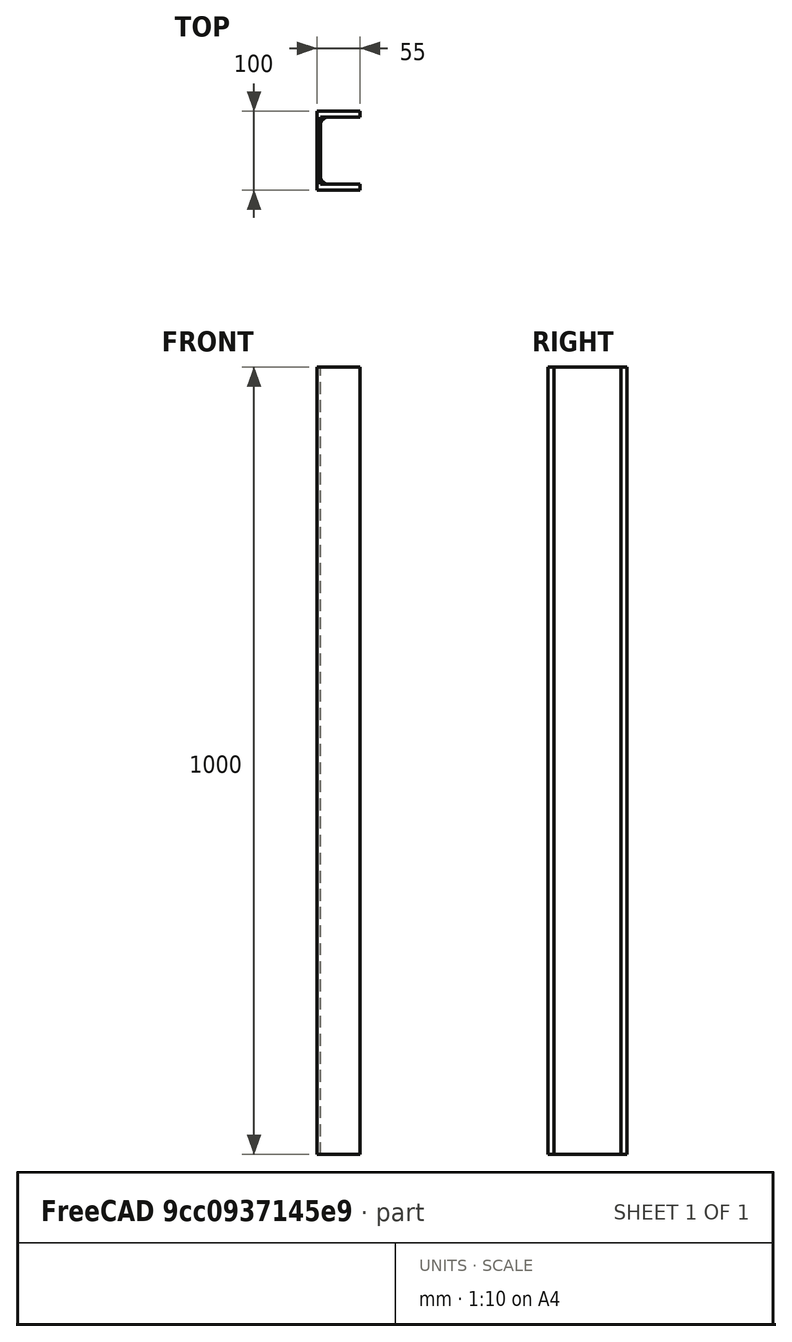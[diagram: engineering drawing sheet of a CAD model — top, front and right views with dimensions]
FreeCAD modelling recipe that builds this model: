
FCSTD DOCUMENT  (FreeCAD 0.21R33694 (Git))
Label: buckling_U100_3D
License: All rights reserved
LicenseURL: http://en.wikipedia.org/wiki/All_rights_reserved
objects: Fem::ConstraintForce×2, Part::Feature×1, Fem::FemSolverObjectPython×1, App::MaterialObjectPython×1, Sketcher::SketchObject×1, Part::Extrusion×1, Fem::ConstraintFixed×1, Fem::FemMeshObjectPython×1, Fem::FemAnalysis×1
note: 3 computed .brp shape members not serialized (recipe doc carries the construction recipe); baked Part::Feature solids carry a one-line shape summary decoded from their .brp

FEATURE [Part::Feature] BOLTS_part  label="UPE100, l=1000.0"
  shape: bbox 55 x 100 x 1000 mm, 12 faces (baked)
FEATURE [Fem::FemSolverObjectPython] SolverCcxTools  # FEM object (typed FeaturePython)
  AnalysisType = 4
  BeamShellResultOutput3D = true
  BucklingFactors = 3
  EigenmodeHighLimit = 1000000
  EigenmodeLowLimit = 0
  EigenmodesCount = 10
  GeometricalNonlinearity = 0
  IterationsControlParameterCutb = 0.25,0.5,0.75,0.85,,,1.5,
  IterationsControlParameterIter = 4,8,9,200,10,400,,200,,
  IterationsControlParameterTimeUse = false
  IterationsThermoMechMaximum = 2000
  IterationsUserDefinedIncrementations = false
  IterationsUserDefinedTimeStepLength = false
  MaterialNonlinearity = 0
  MatrixSolverType = 0
  SplitInputWriter = false
  ThermoMechSteadyState = true
  TimeEnd = 1
  TimeInitialStep = 0.01
FEATURE [App::MaterialObjectPython] MaterialSolid  label="S235"  # material (typed FeaturePython)
  Category = 0
  Material = AuthorAndLicense=(c) 2013 Juergen Riegel (CC-BY 3.0); CardName=CalculiX-Steel; Density=7900 kg/m^3; Description=Standard steel material for CalculiX sample calculations; Father=Metal; Name=CalculiX-Steel; PoissonRatio=0.3; SpecificHeat=590 J/kg/K; ThermalConductivity=43 W/m/K; ThermalExpansionCoefficient=0.000012 m/m/K; YoungsModulus=210000 MPa
FEATURE [Sketcher::SketchObject] Sketch
  ExternalGeometry = -> [BOLTS_part]
  FullyConstrained = true
  MapMode = 5
  Placement = pos=(0,0,0) rot=(1,0,0;3.14159rad)
  Support = -> [BOLTS_part]
  sketch-geometry (9):
    g0: LineSegment StartX=0 StartY=50 StartZ=0 EndX=55 EndY=50 EndZ=0
    g1: LineSegment StartX=55 StartY=42.5 StartZ=0 EndX=55 EndY=50 EndZ=0
    g2: LineSegment StartX=0 StartY=-50 StartZ=0 EndX=0 EndY=0 EndZ=0
    g3: LineSegment StartX=0 StartY=-50 StartZ=0 EndX=55 EndY=-50 EndZ=0
    g4: LineSegment StartX=55 StartY=-50 StartZ=0 EndX=55 EndY=-42.5 EndZ=0
    g5: LineSegment StartX=55 StartY=-42.5 StartZ=0 EndX=4.5 EndY=-42.5 EndZ=0
    g6: LineSegment StartX=55 StartY=42.5 StartZ=0 EndX=4.5 EndY=42.5 EndZ=0
    g7: LineSegment StartX=4.5 StartY=42.5 StartZ=0 EndX=4.5 EndY=-42.5 EndZ=0
    g8: LineSegment StartX=0 StartY=0 StartZ=0 EndX=0 EndY=50 EndZ=0
  constraints (24):
    c: Coincident(g0,g-3)
    c: Coincident(g0,g-3)
    c: Coincident(g1,g0)
    c: Vertical(g1)
    c: PointOnObject(g2,g-2)
    c: Coincident(g2,g-1)
    c: Coincident(g3,g2)
    c: Horizontal(g3)
    c: Coincident(g4,g3)
    c: Vertical(g4)
    c: Coincident(g5,g4)
    c: Horizontal(g5)
    c: Coincident(g6,g1)
    c: Horizontal(g6)
    c: Coincident(g7,g6)
    c: Coincident(g7,g5)
    c: Vertical(g7)
    c: DistanceY(g1,g1) = 7.5
    c: Coincident(g8,g2)
    c: Coincident(g8,g0)
    c: DistanceY(g2,g2) = 50
    c: DistanceX(g0,g6) = 4.5
    c: DistanceY(g4,g4) = 7.5
    c: DistanceX(g3,g3) = 55
FEATURE [Part::Extrusion] Extrude
  Base = -> Sketch
  Dir = (0,0,-1)
  DirMode = 2
  FaceMakerClass = Part::FaceMakerBullseye
  LengthFwd = 0
  LengthRev = 1000
  Solid = true
  Symmetric = false
FEATURE [Fem::ConstraintForce] ConstraintForce  label="N"
  DirectionVector = (0,0,-1)
  Force = 50000
  NormalDirection = (0,0,1)
  Points = (10) [(0,-50,1000),(18.3333,-50,1000),(36.6667,-50,1000),(55,-50,1000),(0,-16.6667,1000),(0,16.6667,1000),(0,50,1000),(18.3333,50,1000),(36.6667,50,1000),(55,50,1000)]
  References = -> [Extrude]
  Reversed = true
  Scale = 8
FEATURE [Fem::ConstraintForce] ConstraintForce001  label="H (p)"
  Direction = -> BOLTS_part [Edge4]
  DirectionVector = (1,0,0)
  Force = 2000
  NormalDirection = (0,0,1)
  Points = (10) [(0,-50,1000),(18.3333,-50,1000),(36.6667,-50,1000),(55,-50,1000),(0,-16.6667,1000),(0,16.6667,1000),(0,50,1000),(18.3333,50,1000),(36.6667,50,1000),(55,50,1000)]
  References = -> [Extrude]
  Scale = 8
FEATURE [Fem::ConstraintFixed] ConstraintFixed001
  NormalDirection = (0,0,-1)
  Normals = (10) [(0,0,-1),(0,0,-1),(0,0,-1),(0,0,-1),(0,0,-1),(0,0,-1),(0,0,-1),(0,0,-1),(0,0,-1),(0,0,-1)]
  Points = (10) [(0,-50,0),(18.3333,-50,0),(36.6667,-50,0),(55,-50,0),(0,-16.6667,0),(0,16.6667,0),(0,50,0),(18.3333,50,0),(36.6667,50,0),(55,50,0)]
  References = -> [Extrude]
  Scale = 8
FEATURE [Fem::FemMeshObjectPython] FEMMeshGmsh  # FEM object (typed FeaturePython)
  Algorithm2D = 0
  Algorithm3D = 0
  CharacteristicLengthMax = 0
  CharacteristicLengthMin = 0
  CoherenceMesh = true
  ElementDimension = 0
  ElementOrder = 1
  GeometryTolerance = 1e-06
  GroupsOfNodes = false
  HighOrderOptimize = 0
  MeshSizeFromCurvature = 12
  OptimizeNetgen = false
  OptimizeStd = true
  Part = -> Extrude
  RecombinationAlgorithm = 0
  Recombine3DAll = false
  RecombineAll = false
  SecondOrderLinear = false
FEATURE [Fem::FemAnalysis] Analysis
  Group = -> [SolverCcxTools,MaterialSolid,ConstraintForce,ConstraintForce001,ConstraintFixed001,FEMMeshGmsh]
